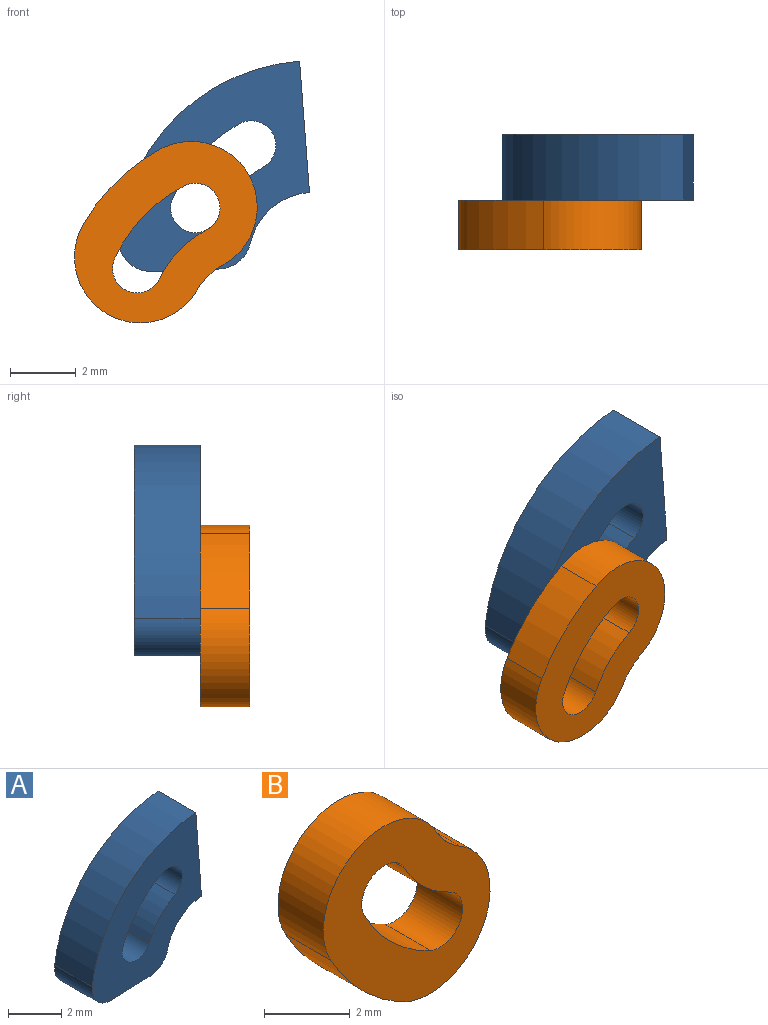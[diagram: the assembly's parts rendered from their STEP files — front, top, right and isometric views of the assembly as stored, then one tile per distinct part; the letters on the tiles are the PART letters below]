
ASSEMBLY  parts=2 mates=1
PART A: 12 faces, bbox 5.8x2x6.4 mm
  f0: cylinder r=0.75mm len=2mm, axis (0,-1,0), area 4.7mm2, adj f1,f9,f10,f11
  f1: cylinder r=3.17mm len=2mm, axis (0,-1,0), area 4.2mm2, adj f0,f2,f10,f11
  f2: cylinder r=0.75mm len=2mm, axis (0,-1,0), area 4.7mm2, adj f1,f9,f10,f11
  f3: cylinder r=2mm len=2mm, axis (0,-1,0), area 5.1mm2, adj f4,f8,f10,f11
  f4: cylinder r=1mm len=2mm, axis (0,-1,0), area 2.6mm2, adj f3,f5,f10,f11
  f5: plane 2.04x2mm, normal (0.04,0,-1), area 4.1mm2, adj f4,f6,f10,f11
  f6: cylinder r=1mm len=2mm, axis (0,-1,0), area 3.5mm2, adj f5,f7,f10,f11
  f7: cylinder r=6mm len=5.51mm, axis (0,-1,0), area 16.5mm2, adj f6,f8,f10,f11
  f8: plane 3.99x2mm, normal (1,0,0.08), area 8mm2, adj f3,f7,f10,f11
  f9: cylinder r=4.67mm len=2.26mm, axis (0,-1,0), area 6.2mm2, adj f0,f2,f10,f11
  f10: plane 6.39x5.81mm, normal (0,1,0), area 19.4mm2, adj f0,f1,f2,f3,f4,f5,f6,f7
  f11: plane 6.39x5.81mm, normal (0,-1,0), area 19.4mm2, adj f0,f1,f2,f3,f4,f5,f6,f7
PART B: 10 faces, bbox 5.5x1.5x5.6 mm
  f0: cylinder r=2mm len=3.76mm, axis (0,1,0), area 9.4mm2, adj f1,f7,f8,f9
  f1: cylinder r=6mm len=2.33mm, axis (0,1,0), area 4.9mm2, adj f0,f2,f8,f9
  f2: cylinder r=2mm len=3.73mm, axis (0,1,0), area 9.4mm2, adj f1,f7,f8,f9
  f3: cylinder r=0.75mm len=1.5mm, axis (0,1,0), area 3.5mm2, adj f4,f6,f8,f9
  f4: cylinder r=4.67mm len=2.18mm, axis (0,1,0), area 4.6mm2, adj f3,f5,f8,f9
  f5: cylinder r=0.75mm len=1.5mm, axis (0,1,0), area 3.5mm2, adj f4,f6,f8,f9
  f6: cylinder r=3.17mm len=1.5mm, axis (0,1,0), area 3.1mm2, adj f3,f5,f8,f9
  f7: cylinder r=2mm len=1.5mm, axis (0,1,0), area 1.6mm2, adj f0,f2,f8,f9
  f8: plane 5.55x5.51mm, normal (0,-1,0), area 15.7mm2, adj f0,f1,f2,f3,f4,f5,f6,f7
  f9: plane 5.55x5.51mm, normal (0,1,0), area 15.7mm2, adj f0,f1,f2,f3,f4,f5,f6,f7
PLACE A t=(6.14,-4.01,9.18)mm
PLACE B rot(axis=(0,1,0),90deg) t=(-0.5,-3.81,-0.83)mm
MATE revolute B.f5 <-> A.f0  axis (0,1,0) through (-4.14,-4.01,9.3)mm
